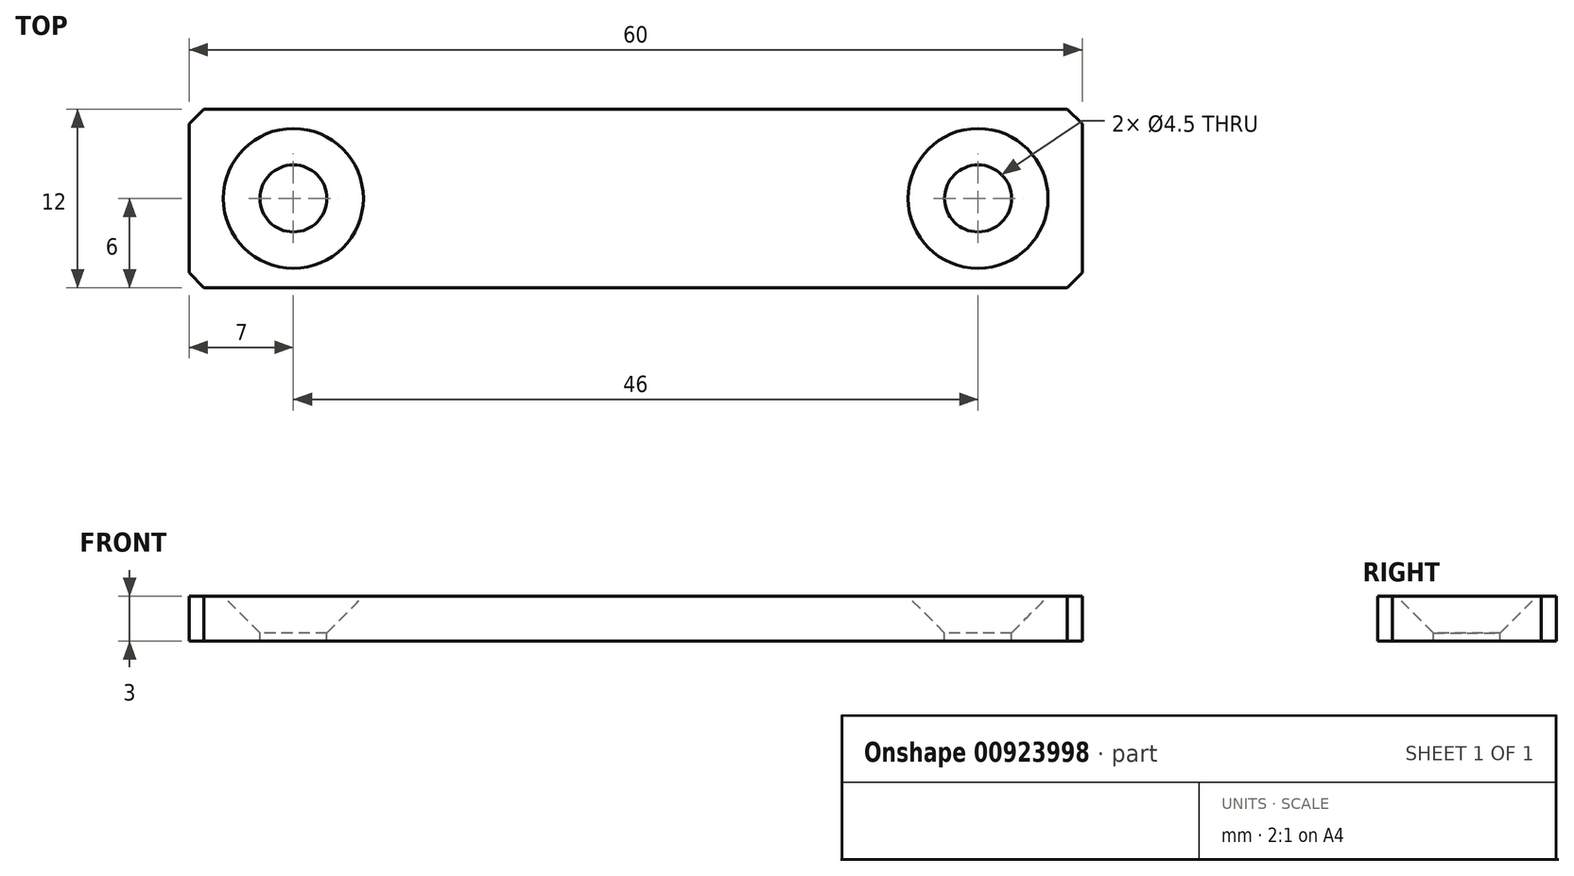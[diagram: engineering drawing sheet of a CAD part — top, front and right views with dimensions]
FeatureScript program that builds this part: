
annotation { "Feature Type Name" : "Feature", "Feature Type Description" : "" }
export const myFeature = defineFeature(function(context is Context, id is Id, definition is map)
    precondition{}
    {
        {
            var Q0;
            Q0=qCreatedBy(makeId("Top.planeOp"),FACE);
            var sketch = newSketch(context, id + "F0", { "sketchPlane" : qUnion([Q0])});
            skLineSegment(sketch, "E0.bottom", {"start": v(30, -6) * mm, "end": v(-30, -6) * mm});
            skLineSegment(sketch, "E0.top", {"start": v(30, 6) * mm, "end": v(-30, 6) * mm});
            skLineSegment(sketch, "E0.left", {"start": v(30, -6) * mm, "end": v(30, 6) * mm});
            skLineSegment(sketch, "E0.right", {"start": v(-30, -6) * mm, "end": v(-30, 6) * mm});
            skPoint(sketch, "E0.middle", {"position": v(0, 0) * mm});
            skSolve(sketch);
        }
        {
            var Q0;
            Q0 = qSketchRegion(id + "F0", true);
            extrude(context, id + "F1", {"entities" : qUnion([Q0]), "depth" : 3 * mm, "offsetDistance" : 25 * mm});
        }
        {
            var Q0;
            Q0=makeQuery(id+"F1.opExtrude","CAP_FACE",FACE,{"disambiguationData":[OSD([sQuery(id+"F0.wireOp",EDGE,"E0.bottom"),sQuery(id+"F0.wireOp",EDGE,"E0.top"),sQuery(id+"F0.wireOp",EDGE,"E0.left"),sQuery(id+"F0.wireOp",EDGE,"E0.right")])],"isStart":false});
            var sketch = newSketch(context, id + "F2", { "sketchPlane" : qUnion([Q0])});
            skPoint(sketch, "E1", {"position": v(-23, 0) * mm});
            skPoint(sketch, "E1.positionSnap0", {"position": v(-30, 0) * mm});
            skPoint(sketch, "E2", {"position": v(23, 0) * mm});
            skSolve(sketch);
        }
        {
            var Q0;
            Q0=sQuery(id+"F2.wireOp",VERTEX,"E1");
            var Q1;
            Q1=sQuery(id+"F2.wireOp",VERTEX,"E2");
            var Q2;
            Q2=makeQuery(id+"F1.opExtrude","SWEPT_BODY",BODY,{"disambiguationData":[OSD([sQuery(id+"F0.wireOp",EDGE,"E0.bottom"),sQuery(id+"F0.wireOp",EDGE,"E0.top"),sQuery(id+"F0.wireOp",EDGE,"E0.left"),sQuery(id+"F0.wireOp",EDGE,"E0.right")])]});
            hole(context, id + "F3", {"style" : HoleStyle.C_SINK, "endStyle" : HoleEndStyle.BLIND, "standardTappedOrClearance" : lookupTablePath({ "standard" : "ISO", "size" : "4.5", "type" : "Drilled" }), "standardBlindInLast" : lookupTablePath({ "standard" : "ISO", "size" : "4.5", "type" : "Drilled" }), "holeDiameter" : 4.5 * mm, "cSinkDiameter" : 9.4 * mm, "cSinkAngle" : 90 * degree, "majorDiameter" : 4 * mm, "holeDepth" : 3.4 * mm, "isTappedThrough" : true, "tappedDepth" : 9 * mm, "tapClearance" : 3, "startFromSketch" : true, "locations" : qUnion([Q0, Q1]), "scope" : qUnion([Q2])});
        }
        {
            var Q0;
            Q0=makeQuery(id+"F1.opExtrude","SWEPT_EDGE",EDGE,{"disambiguationData":[OSD([sQuery(id+"F0.wireOp",EDGE,"E0.top"),sQuery(id+"F0.wireOp",EDGE,"E0.left")])]});
            var Q1;
            Q1=makeQuery(id+"F1.opExtrude","SWEPT_EDGE",EDGE,{"disambiguationData":[OSD([sQuery(id+"F0.wireOp",EDGE,"E0.bottom"),sQuery(id+"F0.wireOp",EDGE,"E0.left")])]});
            var Q2;
            Q2=makeQuery(id+"F1.opExtrude","SWEPT_EDGE",EDGE,{"disambiguationData":[OSD([sQuery(id+"F0.wireOp",EDGE,"E0.bottom"),sQuery(id+"F0.wireOp",EDGE,"E0.right")])]});
            var Q3;
            Q3=makeQuery(id+"F1.opExtrude","SWEPT_EDGE",EDGE,{"disambiguationData":[OSD([sQuery(id+"F0.wireOp",EDGE,"E0.top"),sQuery(id+"F0.wireOp",EDGE,"E0.right")])]});
            chamfer(context, id + "F4", {"entities" : qUnion([Q0, Q1, Q2, Q3]), "width" : 1 * mm, "tangentPropagation" : true});
        }
    });
